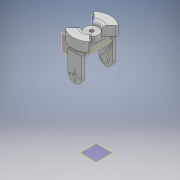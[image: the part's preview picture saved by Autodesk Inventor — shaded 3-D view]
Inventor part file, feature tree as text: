
AUTODESK INVENTOR PART (.ipt)
format: ipt  version: 2018 (Build 220112000, 112)  size: 264,192 bytes
history: native  units: mm
features: extrude x9, sketch x9, plane x4, fillet x4, other x3
ambient origin geometry x8: Origin, YZ Plane, XZ Plane, XY Plane, X Axis, Y Axis, Z Axis, Center Point
bodies: Solid1 (feature_tree)
feature tree (29):
  extrude  "base"  Depth=18.0mm
  plane  "Work Plane1"
  plane  "Work Plane2"
  extrude  "connector_prev_servo"  [1 undecoded]
  fillet  "Fillet3"  Radius=4.0mm
  plane  "Work Plane6"
  extrude  "screw_holes"  Depth=9.0mm TaperAngle=0.0deg
  fillet  "Fillet4"  Radius=9.0mm
  plane  "Work Plane7"
  extrude  "Extrusion14"  Depth=6.0mm
  extrude  "Extrusion26"  Depth=20.0mm TaperAngle=360.0deg
  fillet  "Fillet6"  Radius=20.0mm
  extrude  "Extrusion27"  Depth=6.0mm
  fillet  "Fillet7"  Radius=6.0mm
  extrude  "Extrusion28"  Depth=40.0mm
  extrude  "Extrusion29"  Depth=18.0mm
  other  "Edición directa1"
  extrude  "Extrusión30"  Depth=2.0mm
  sketch  "Sketch1"  dims[d0=18.0mm d1=32.0mm]
  sketch  "Sketch12"  dims[d2=15.0mm d3=0.0mm d63=-10.0mm d64=4.0mm]
  sketch  "Sketch13"  dims[d65=4.0mm d66=36.0mm d67=0.0mm d71=9.0mm]
  sketch  "Sketch14"  dims[d72=5.5mm d73=6.0mm]
  sketch  "Sketch26"  dims[d74=2.0mm d75=40.0mm d77=360.0deg d79=20.0mm d80=0.0mm]
  sketch  "Sketch27"  dims[d81=9.0mm d82=10.5mm d83=6.0mm d84=0.0mm]
  sketch  "Sketch28"  dims[d154=50.0mm d155=40.0mm]
  sketch  "Sketch29"  dims[d156=40.0mm d157=18.0mm]
  sketch  "Boceto30"  dims[d158=13.0mm d159=0.0mm d160=2.0mm d161=5.0mm d162=0.0mm d163=5.0mm d164=5.0mm d165=5.0mm d166=0.0mm d167=25.0mm d168=49.7mm d169=60.0mm d170=10.0mm d171=0.0mm d172=0.0mm d173=0.0mm d174=2.5mm d175=0.0mm d176=0.0mm d177=-2.5mm d178=9.5mm d179=2.0mm d180=0.0mm]
  other  "Desplazar1"
  other  "Desplazar2"
note: 1 required parameter value undecoded (feature->parameter linkage not recoverable at this tier; creation-order binding heuristic only, values carry confidence <= 0.55)
